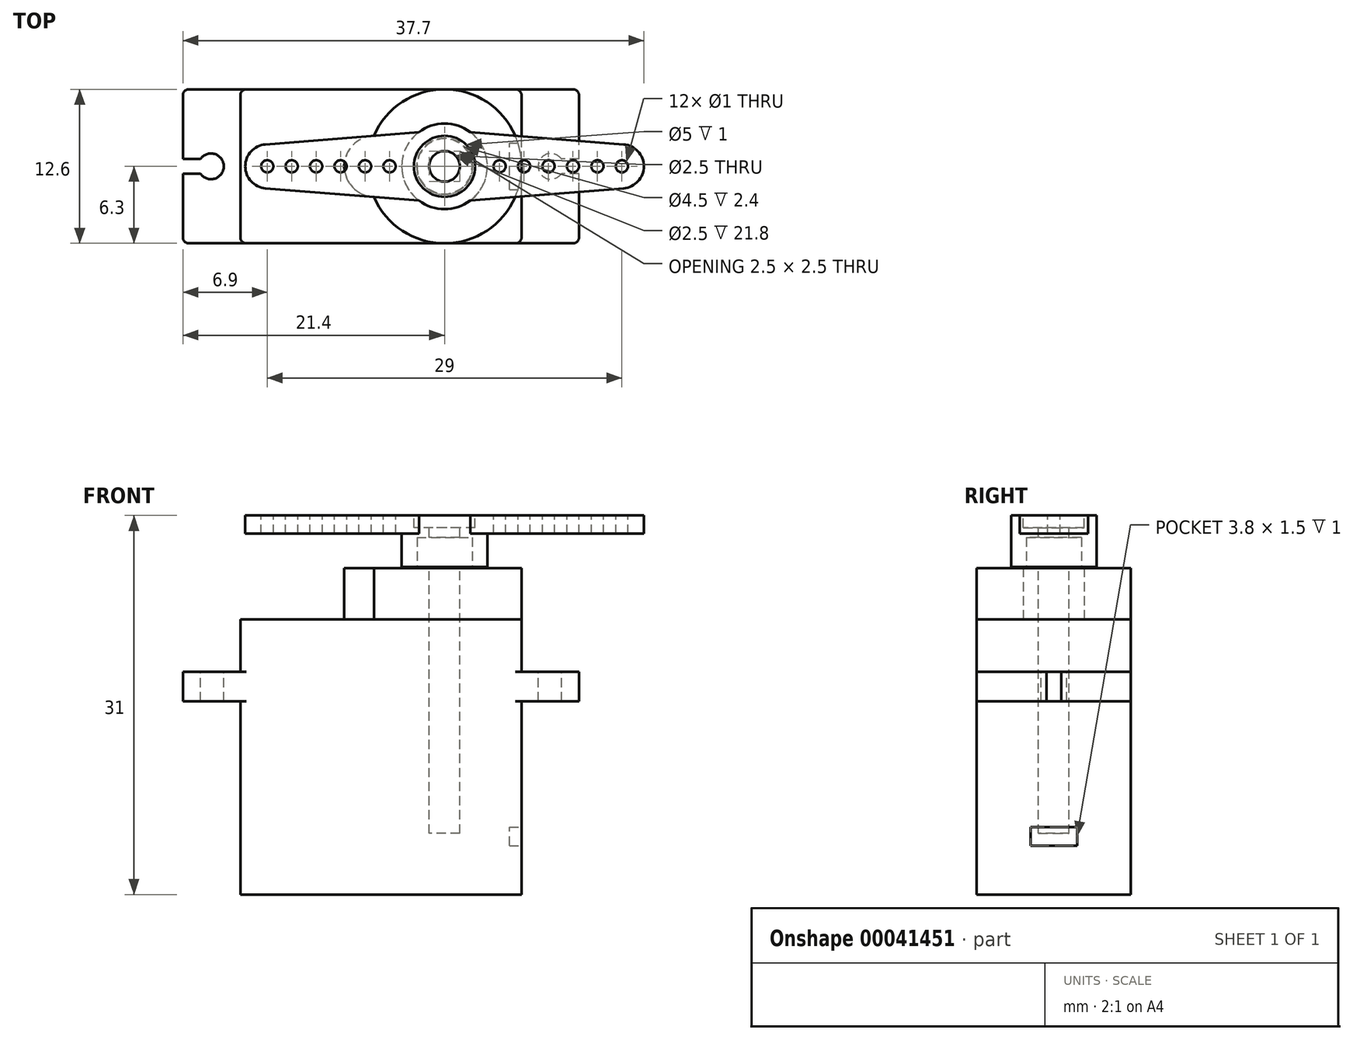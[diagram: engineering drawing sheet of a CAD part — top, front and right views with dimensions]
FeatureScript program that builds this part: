
annotation { "Feature Type Name" : "Feature", "Feature Type Description" : "" }
export const myFeature = defineFeature(function(context is Context, id is Id, definition is map)
    precondition{}
    {
        {
            var Q0;
            Q0=qCreatedBy(makeId("Front.planeOp"),FACE);
            var sketch = newSketch(context, id + "F0", { "sketchPlane" : qUnion([Q0])});
            skLineSegment(sketch, "E0.bottom", {"start": v(0, 0) * mm, "end": v(23, 0) * mm});
            skLineSegment(sketch, "E0.top", {"start": v(0, 22.5) * mm, "end": v(23, 22.5) * mm});
            skLineSegment(sketch, "E0.left", {"start": v(0, 0) * mm, "end": v(0, 22.5) * mm});
            skLineSegment(sketch, "E0.right", {"start": v(23, 0) * mm, "end": v(23, 22.5) * mm});
            skLineSegment(sketch, "E1.bottom", {"start": v(0, 15.8) * mm, "end": v(-4.7, 15.8) * mm});
            skLineSegment(sketch, "E1.top", {"start": v(0, 18.2) * mm, "end": v(-4.7, 18.2) * mm});
            skLineSegment(sketch, "E1.left", {"start": v(0, 15.8) * mm, "end": v(0, 18.2) * mm});
            skLineSegment(sketch, "E1.right", {"start": v(-4.7, 15.8) * mm, "end": v(-4.7, 18.2) * mm});
            skLineSegment(sketch, "E2", {"start": v(11.5, 0) * mm, "end": v(11.5, 38.16) * mm, "construction": true});
            skLineSegment(sketch, "E3.0.MirrorCS", {"start": v(27.7, 15.8) * mm, "end": v(27.7, 18.2) * mm});
            skLineSegment(sketch, "E4.0.MirrorCS", {"start": v(23, 18.2) * mm, "end": v(27.7, 18.2) * mm});
            skLineSegment(sketch, "E5.0.MirrorCS", {"start": v(23, 15.8) * mm, "end": v(27.7, 15.8) * mm});
            skSolve(sketch);
        }
        {
            var Q0;
            Q0=qSketchRegion(id+"F0",true);
            extrude(context, id + "F1", {"entities" : qUnion([Q0]), "depth" : 12.6 * mm});
        }
        {
            var Q0;
            Q0=makeQuery(id+"F1.opExtrude","SWEPT_FACE",FACE,{"disambiguationData":[OSD([sQuery(id+"F0.wireOp",EDGE,"E0.top")])]});
            var sketch = newSketch(context, id + "F2", { "sketchPlane" : qUnion([Q0])});
            skLineSegment(sketch, "E6", {"start": v(23, -6.3) * mm, "end": v(0, -6.3) * mm, "construction": true});
            skArc(sketch, "E7", {"start": v(10.92, -8.8) * mm, "mid": v(23, -6.3) * mm, "end": v(10.92, -3.8) * mm});
            skArc(sketch, "E8", {"start": v(10.92, -3.8) * mm, "mid": v(8.5, -6.3) * mm, "end": v(10.92, -8.8) * mm});
            skSolve(sketch);
        }
        {
            var Q0;
            Q0=qSketchRegion(id+"F2",true);
            extrude(context, id + "F3", {"entities" : qUnion([Q0]), "operationType" : NewBodyOperationType.ADD, "depth" : (26.7 - 22.5) * mm});
        }
        {
            var Q0;
            Q0=makeQuery(id+"F3.opExtrude","CAP_FACE",FACE,{"disambiguationData":[OSD([sQuery(id+"F2.wireOp",EDGE,"E7"),sQuery(id+"F2.wireOp",EDGE,"E8")])],"isStart":false});
            var sketch = newSketch(context, id + "F4", { "sketchPlane" : qUnion([Q0])});
            skCircle(sketch, "E9", {"center": v(16.7, -6.3) * mm, "radius": 0.9 * mm});
            skCircle(sketch, "E10", {"center": v(16.7, -6.3) * mm, "radius": 2.3 * mm});
            skSolve(sketch);
        }
        {
            var Q0;
            Q0=qSketchRegion(id+"F4",true);
            extrude(context, id + "F5", {"entities" : qUnion([Q0]), "operationType" : NewBodyOperationType.ADD, "depth" : (29.2 - 26.7) * mm});
        }
        {
            var Q0;
            Q0=makeQuery(id+"F1.opExtrude","SWEPT_FACE",FACE,{"disambiguationData":[OSD([sQuery(id+"F0.wireOp",EDGE,"E1.top")])]});
            var sketch = newSketch(context, id + "F6", { "sketchPlane" : qUnion([Q0])});
            skLineSegment(sketch, "E11", {"start": v(-4.7, -6.3) * mm, "end": v(30.63, -6.3) * mm, "construction": true});
            skLineSegment(sketch, "E12.0", {"start": v(0, -12.6) * mm, "end": v(23, -12.6) * mm, "construction": true});
            skLineSegment(sketch, "E13.0", {"start": v(0, 0) * mm, "end": v(23, 0) * mm, "construction": true});
            skLineSegment(sketch, "E14", {"start": v(11.5, 0) * mm, "end": v(11.5, -12.6) * mm, "construction": true});
            skArc(sketch, "E15", {"start": v(-3.26, -6.9) * mm, "mid": v(-1.35, -6.3) * mm, "end": v(-3.26, -5.7) * mm});
            skArc(sketch, "E16.0.MirrorC", {"start": v(26.26, -6.9) * mm, "mid": v(24.35, -6.3) * mm, "end": v(26.26, -5.7) * mm});
            skLineSegment(sketch, "E17.bottom", {"start": v(-5.39, -6.9) * mm, "end": v(-3.26, -6.9) * mm});
            skLineSegment(sketch, "E17.top", {"start": v(-5.39, -5.7) * mm, "end": v(-3.26, -5.7) * mm});
            skLineSegment(sketch, "E17.left", {"start": v(-5.39, -6.9) * mm, "end": v(-5.39, -5.7) * mm});
            skLineSegment(sketch, "E18.0.MirrorCS", {"start": v(28.39, -6.9) * mm, "end": v(26.26, -6.9) * mm});
            skLineSegment(sketch, "E18.1.MirrorCS", {"start": v(28.39, -5.7) * mm, "end": v(26.26, -5.7) * mm});
            skLineSegment(sketch, "E18.3.MirrorCS", {"start": v(28.39, -6.9) * mm, "end": v(28.39, -5.7) * mm});
            skSolve(sketch);
        }
        {
            var Q0;
            Q0=qSketchRegion(id+"F6",true);
            extrude(context, id + "F7", {"entities" : qUnion([Q0]), "operationType" : NewBodyOperationType.REMOVE, "oppositeDirection" : true, "depth" : 25 * mm});
        }
        {
            var Q0;
            {var subQ0=sQuery(id+"F0.wireOp",EDGE,"E0.left");Q0=makeQuery(id+"F1.opExtrude","CAP_EDGE",EDGE,{"disambiguationData":[OSD([subQ0]),TDD([makeQuery(id+"F0.imprint","IMPRINT",EDGE,{"disambiguationData":[TD([[makeQuery(id+"F0.imprint","INTERSECT",VERTEX,{"derivedFrom":[sQuery(id+"F0.wireOp",EDGE,"E0.top"),subQ0]}),1.0]])],"derivedFrom":subQ0})])],"isStart":false});}
            var Q1;
            {var subQ0=sQuery(id+"F0.wireOp",EDGE,"E0.left");Q1=makeQuery(id+"F1.opExtrude","CAP_EDGE",EDGE,{"disambiguationData":[OSD([subQ0]),TDD([makeQuery(id+"F0.imprint","IMPRINT",EDGE,{"disambiguationData":[TD([[makeQuery(id+"F0.imprint","INTERSECT",VERTEX,{"derivedFrom":[sQuery(id+"F0.wireOp",EDGE,"E0.bottom"),subQ0]}),-1.0]])],"derivedFrom":subQ0})])],"isStart":false});}
            var Q2;
            {var subQ0=sQuery(id+"F0.wireOp",EDGE,"E0.left");Q2=makeQuery(id+"F1.opExtrude","CAP_EDGE",EDGE,{"disambiguationData":[OSD([subQ0]),TDD([makeQuery(id+"F0.imprint","IMPRINT",EDGE,{"disambiguationData":[TD([[makeQuery(id+"F0.imprint","INTERSECT",VERTEX,{"derivedFrom":[sQuery(id+"F0.wireOp",EDGE,"E0.top"),subQ0]}),1.0]])],"derivedFrom":subQ0})])],"isStart":true});}
            var Q3;
            {var subQ0=sQuery(id+"F0.wireOp",EDGE,"E0.left");Q3=makeQuery(id+"F1.opExtrude","CAP_EDGE",EDGE,{"disambiguationData":[OSD([subQ0]),TDD([makeQuery(id+"F0.imprint","IMPRINT",EDGE,{"disambiguationData":[TD([[makeQuery(id+"F0.imprint","INTERSECT",VERTEX,{"derivedFrom":[sQuery(id+"F0.wireOp",EDGE,"E0.bottom"),subQ0]}),-1.0]])],"derivedFrom":subQ0})])],"isStart":true});}
            var Q4;
            Q4=makeQuery(id+"F1.opExtrude","CAP_EDGE",EDGE,{"disambiguationData":[OSD([sQuery(id+"F0.wireOp",EDGE,"E1.right")])],"isStart":false});
            var Q5;
            Q5=makeQuery(id+"F1.opExtrude","CAP_EDGE",EDGE,{"disambiguationData":[OSD([sQuery(id+"F0.wireOp",EDGE,"E1.right")])],"isStart":true});
            var Q6;
            Q6=makeQuery(id+"F1.opExtrude","CAP_EDGE",EDGE,{"disambiguationData":[OSD([sQuery(id+"F0.wireOp",EDGE,"E3.0.MirrorCS")])],"isStart":false});
            var Q7;
            {var subQ0=sQuery(id+"F0.wireOp",EDGE,"E0.right");Q7=makeQuery(id+"F1.opExtrude","CAP_EDGE",EDGE,{"disambiguationData":[OSD([subQ0]),TDD([makeQuery(id+"F0.imprint","IMPRINT",EDGE,{"disambiguationData":[TD([[makeQuery(id+"F0.imprint","INTERSECT",VERTEX,{"derivedFrom":[sQuery(id+"F0.wireOp",EDGE,"E0.top"),subQ0]}),1.0]])],"derivedFrom":subQ0})])],"isStart":false});}
            var Q8;
            {var subQ0=sQuery(id+"F0.wireOp",EDGE,"E0.right");Q8=makeQuery(id+"F1.opExtrude","CAP_EDGE",EDGE,{"disambiguationData":[OSD([subQ0]),TDD([makeQuery(id+"F0.imprint","IMPRINT",EDGE,{"disambiguationData":[TD([[makeQuery(id+"F0.imprint","INTERSECT",VERTEX,{"derivedFrom":[sQuery(id+"F0.wireOp",EDGE,"E0.bottom"),subQ0]}),-1.0]])],"derivedFrom":subQ0})])],"isStart":false});}
            var Q9;
            Q9=makeQuery(id+"F1.opExtrude","CAP_EDGE",EDGE,{"disambiguationData":[OSD([sQuery(id+"F0.wireOp",EDGE,"E3.0.MirrorCS")])],"isStart":true});
            var Q10;
            {var subQ0=sQuery(id+"F0.wireOp",EDGE,"E0.right");Q10=makeQuery(id+"F1.opExtrude","CAP_EDGE",EDGE,{"disambiguationData":[OSD([subQ0]),TDD([makeQuery(id+"F0.imprint","IMPRINT",EDGE,{"disambiguationData":[TD([[makeQuery(id+"F0.imprint","INTERSECT",VERTEX,{"derivedFrom":[sQuery(id+"F0.wireOp",EDGE,"E0.top"),subQ0]}),1.0]])],"derivedFrom":subQ0})])],"isStart":true});}
            var Q11;
            {var subQ0=sQuery(id+"F0.wireOp",EDGE,"E0.right");Q11=makeQuery(id+"F1.opExtrude","CAP_EDGE",EDGE,{"disambiguationData":[OSD([subQ0]),TDD([makeQuery(id+"F0.imprint","IMPRINT",EDGE,{"disambiguationData":[TD([[makeQuery(id+"F0.imprint","INTERSECT",VERTEX,{"derivedFrom":[sQuery(id+"F0.wireOp",EDGE,"E0.bottom"),subQ0]}),-1.0]])],"derivedFrom":subQ0})])],"isStart":true});}
            fillet(context, id + "F8", {"entities" : qUnion([Q0, Q1, Q2, Q3, Q4, Q5, Q6, Q7, Q8, Q9, Q10, Q11]), "radius" : 0.5 * mm, "tangentPropagation" : true, "allowEdgeOverflow" : false});
        }
        {
            var Q0;
            {var subQ0=sQuery(id+"F0.wireOp",EDGE,"E0.right");Q0=makeQuery(id+"F1.opExtrude","SWEPT_FACE",FACE,{"disambiguationData":[OSD([subQ0]),TDD([makeQuery(id+"F0.imprint","IMPRINT",EDGE,{"disambiguationData":[TD([[makeQuery(id+"F0.imprint","INTERSECT",VERTEX,{"derivedFrom":[sQuery(id+"F0.wireOp",EDGE,"E0.bottom"),subQ0]}),-1.0]])],"derivedFrom":subQ0})])]});}
            var sketch = newSketch(context, id + "F9", { "sketchPlane" : qUnion([Q0])});
            skLineSegment(sketch, "E19.bottom", {"start": v(-8.2, 4) * mm, "end": v(-4.4, 4) * mm});
            skLineSegment(sketch, "E19.top", {"start": v(-8.2, 5.5) * mm, "end": v(-4.4, 5.5) * mm});
            skLineSegment(sketch, "E19.left", {"start": v(-8.2, 4) * mm, "end": v(-8.2, 5.5) * mm});
            skLineSegment(sketch, "E19.right", {"start": v(-4.4, 4) * mm, "end": v(-4.4, 5.5) * mm});
            skLineSegment(sketch, "E20", {"start": v(-6.3, 0) * mm, "end": v(-6.3, 11.49) * mm, "construction": true});
            skSolve(sketch);
        }
        {
            var Q0;
            Q0=qSketchRegion(id+"F9",true);
            extrude(context, id + "F10", {"entities" : qUnion([Q0]), "operationType" : NewBodyOperationType.REMOVE, "oppositeDirection" : true, "depth" : 1 * mm});
        }
        {
            var Q0;
            Q0=makeQuery(id+"F1.opExtrude","SWEPT_FACE",FACE,{"disambiguationData":[OSD([sQuery(id+"F0.wireOp",EDGE,"E0.bottom")])]});
            cPlane(context, id + "F11", {"entities" : qUnion([Q0]), "cplaneType" : CPlaneType.OFFSET, "offset" : 31 * mm, "oppositeDirection" : true, "width" : 150 * mm, "height" : 150 * mm});
        }
        {
            var Q0;
            Q0=qCreatedBy(id+"F11.planeOp",FACE);
            var sketch = newSketch(context, id + "F12", { "sketchPlane" : qUnion([Q0])});
            skCircle(sketch, "E21.0", {"center": v(16.7, 6.3) * mm, "radius": 2.3 * mm, "construction": true});
            skArc(sketch, "E22", {"start": v(14.6, 3.5) * mm, "mid": v(16.7, 2.8) * mm, "end": v(18.8, 3.5) * mm});
            skCircle(sketch, "E23", {"center": v(16.7, 6.3) * mm, "radius": 14.5 * mm, "construction": true});
            skLineSegment(sketch, "E24", {"start": v(2.2, 6.3) * mm, "end": v(31.2, 6.3) * mm, "construction": true});
            skCircle(sketch, "E25", {"center": v(2.2, 6.3) * mm, "radius": 0.5 * mm});
            skArc(sketch, "E26", {"start": v(2.06, 8.1) * mm, "mid": v(0.4, 6.3) * mm, "end": v(2.06, 4.5) * mm});
            skLineSegment(sketch, "E27", {"start": v(2.06, 4.5) * mm, "end": v(14.6, 3.5) * mm});
            skLineSegment(sketch, "E28.0", {"start": v(2.2, 3.5) * mm, "end": v(31.2, 3.5) * mm, "construction": true});
            skLineSegment(sketch, "E29.0.MirrorCS", {"start": v(2.06, 8.1) * mm, "end": v(14.6, 9.1) * mm});
            skCircle(sketch, "E30.1.0.0", {"center": v(4.2, 6.3) * mm, "radius": 0.5 * mm});
            skCircle(sketch, "E30.2.0.0", {"center": v(6.2, 6.3) * mm, "radius": 0.5 * mm});
            skCircle(sketch, "E30.3.0.0", {"center": v(8.2, 6.3) * mm, "radius": 0.5 * mm});
            skCircle(sketch, "E30.4.0.0", {"center": v(10.2, 6.3) * mm, "radius": 0.5 * mm});
            skCircle(sketch, "E30.5.0.0", {"center": v(12.2, 6.3) * mm, "radius": 0.5 * mm});
            skLineSegment(sketch, "E30.direction1", {"start": v(2.2, 6.3) * mm, "end": v(4.2, 6.3) * mm, "construction": true});
            skLineSegment(sketch, "E31", {"start": v(16.7, -0.68) * mm, "end": v(16.7, 13.17) * mm, "construction": true});
            skLineSegment(sketch, "E32.0.MirrorCS", {"start": v(31.34, 4.5) * mm, "end": v(18.8, 3.5) * mm});
            skArc(sketch, "E33.0.MirrorCS", {"start": v(31.34, 8.1) * mm, "mid": v(33, 6.3) * mm, "end": v(31.34, 4.5) * mm});
            skLineSegment(sketch, "E34.0.MirrorCS", {"start": v(31.34, 8.1) * mm, "end": v(18.8, 9.1) * mm});
            skCircle(sketch, "E35.0.MirrorC", {"center": v(31.2, 6.3) * mm, "radius": 0.5 * mm});
            skCircle(sketch, "E36.0.MirrorC", {"center": v(29.2, 6.3) * mm, "radius": 0.5 * mm});
            skCircle(sketch, "E37.0.MirrorC", {"center": v(27.2, 6.3) * mm, "radius": 0.5 * mm});
            skCircle(sketch, "E38.0.MirrorC", {"center": v(25.2, 6.3) * mm, "radius": 0.5 * mm});
            skCircle(sketch, "E39.0.MirrorC", {"center": v(23.2, 6.3) * mm, "radius": 0.5 * mm});
            skCircle(sketch, "E40.0.MirrorC", {"center": v(21.2, 6.3) * mm, "radius": 0.5 * mm});
            skArc(sketch, "E41.trimOffspring", {"start": v(18.8, 9.1) * mm, "mid": v(16.7, 9.8) * mm, "end": v(14.6, 9.1) * mm});
            skSolve(sketch);
        }
        {
            var Q0;
            Q0=qSketchRegion(id+"F12",true);
            extrude(context, id + "F13", {"entities" : qUnion([Q0]), "depth" : 1.5 * mm});
        }
        {
            var Q0;
            Q0=makeQuery(id+"F13.opExtrude","CAP_FACE",FACE,{"disambiguationData":[OSD([sQuery(id+"F12.wireOp",EDGE,"E22"),sQuery(id+"F12.wireOp",EDGE,"E25"),sQuery(id+"F12.wireOp",EDGE,"E26"),sQuery(id+"F12.wireOp",EDGE,"E27"),sQuery(id+"F12.wireOp",EDGE,"E29.0.MirrorCS"),sQuery(id+"F12.wireOp",EDGE,"E30.1.0.0"),sQuery(id+"F12.wireOp",EDGE,"E30.2.0.0"),sQuery(id+"F12.wireOp",EDGE,"E30.3.0.0"),sQuery(id+"F12.wireOp",EDGE,"E30.4.0.0"),sQuery(id+"F12.wireOp",EDGE,"E30.5.0.0"),sQuery(id+"F12.wireOp",EDGE,"E32.0.MirrorCS"),sQuery(id+"F12.wireOp",EDGE,"E33.0.MirrorCS"),sQuery(id+"F12.wireOp",EDGE,"E34.0.MirrorCS"),sQuery(id+"F12.wireOp",EDGE,"E35.0.MirrorC"),sQuery(id+"F12.wireOp",EDGE,"E36.0.MirrorC"),sQuery(id+"F12.wireOp",EDGE,"E37.0.MirrorC"),sQuery(id+"F12.wireOp",EDGE,"E38.0.MirrorC"),sQuery(id+"F12.wireOp",EDGE,"E39.0.MirrorC"),sQuery(id+"F12.wireOp",EDGE,"E40.0.MirrorC"),sQuery(id+"F12.wireOp",EDGE,"E41.trimOffspring")])],"isStart":false});
            var sketch = newSketch(context, id + "F14", { "sketchPlane" : qUnion([Q0])});
            skCircle(sketch, "E42", {"center": v(16.7, 6.3) * mm, "radius": 3.5 * mm});
            skSolve(sketch);
        }
        {
            var Q0;
            Q0=qSketchRegion(id+"F14",true);
            extrude(context, id + "F15", {"entities" : qUnion([Q0]), "operationType" : NewBodyOperationType.ADD, "depth" : (4.2 - 1.5) * mm});
        }
        {
            var Q0;
            Q0=makeQuery(id+"F15.opExtrude","CAP_FACE",FACE,{"disambiguationData":[OSD([sQuery(id+"F14.wireOp",EDGE,"E42")])],"isStart":false});
            var sketch = newSketch(context, id + "F16", { "sketchPlane" : qUnion([Q0])});
            skCircle(sketch, "E43", {"center": v(16.7, 6.3) * mm, "radius": 2.25 * mm});
            skSolve(sketch);
        }
        {
            var Q0;
            Q0=qSketchRegion(id+"F16",true);
            extrude(context, id + "F17", {"entities" : qUnion([Q0]), "operationType" : NewBodyOperationType.REMOVE, "oppositeDirection" : true, "depth" : 2.4 * mm});
        }
        {
            var Q0;
            Q0=makeQuery(id+"F13.opExtrude","CAP_FACE",FACE,{"disambiguationData":[OSD([sQuery(id+"F12.wireOp",EDGE,"E22"),sQuery(id+"F12.wireOp",EDGE,"E25"),sQuery(id+"F12.wireOp",EDGE,"E26"),sQuery(id+"F12.wireOp",EDGE,"E27"),sQuery(id+"F12.wireOp",EDGE,"E29.0.MirrorCS"),sQuery(id+"F12.wireOp",EDGE,"E30.1.0.0"),sQuery(id+"F12.wireOp",EDGE,"E30.2.0.0"),sQuery(id+"F12.wireOp",EDGE,"E30.3.0.0"),sQuery(id+"F12.wireOp",EDGE,"E30.4.0.0"),sQuery(id+"F12.wireOp",EDGE,"E30.5.0.0"),sQuery(id+"F12.wireOp",EDGE,"E32.0.MirrorCS"),sQuery(id+"F12.wireOp",EDGE,"E33.0.MirrorCS"),sQuery(id+"F12.wireOp",EDGE,"E34.0.MirrorCS"),sQuery(id+"F12.wireOp",EDGE,"E35.0.MirrorC"),sQuery(id+"F12.wireOp",EDGE,"E36.0.MirrorC"),sQuery(id+"F12.wireOp",EDGE,"E37.0.MirrorC"),sQuery(id+"F12.wireOp",EDGE,"E38.0.MirrorC"),sQuery(id+"F12.wireOp",EDGE,"E39.0.MirrorC"),sQuery(id+"F12.wireOp",EDGE,"E40.0.MirrorC"),sQuery(id+"F12.wireOp",EDGE,"E41.trimOffspring")])],"isStart":true});
            var sketch = newSketch(context, id + "F18", { "sketchPlane" : qUnion([Q0])});
            skCircle(sketch, "E44", {"center": v(16.7, -6.3) * mm, "radius": 2.5 * mm});
            skSolve(sketch);
        }
        {
            var Q0;
            Q0=qSketchRegion(id+"F18",true);
            extrude(context, id + "F19", {"entities" : qUnion([Q0]), "operationType" : NewBodyOperationType.REMOVE, "oppositeDirection" : true, "depth" : 1 * mm});
        }
        {
            var Q0;
            Q0=makeQuery(id+"F19.boolean.opBoolean","COPY",FACE,{"derivedFrom":makeQuery(id+"F19.opExtrude","CAP_FACE",FACE,{"disambiguationData":[OSD([sQuery(id+"F18.wireOp",EDGE,"E44")])],"isStart":false})});
            var sketch = newSketch(context, id + "F20", { "sketchPlane" : qUnion([Q0])});
            skCircle(sketch, "E45", {"center": v(16.7, -6.3) * mm, "radius": 1.25 * mm});
            skSolve(sketch);
        }
        {
            var Q0;
            Q0=qSketchRegion(id+"F20",true);
            extrude(context, id + "F21", {"entities" : qUnion([Q0]), "operationType" : NewBodyOperationType.REMOVE, "oppositeDirection" : true, "depth" : 25 * mm});
        }
    });
